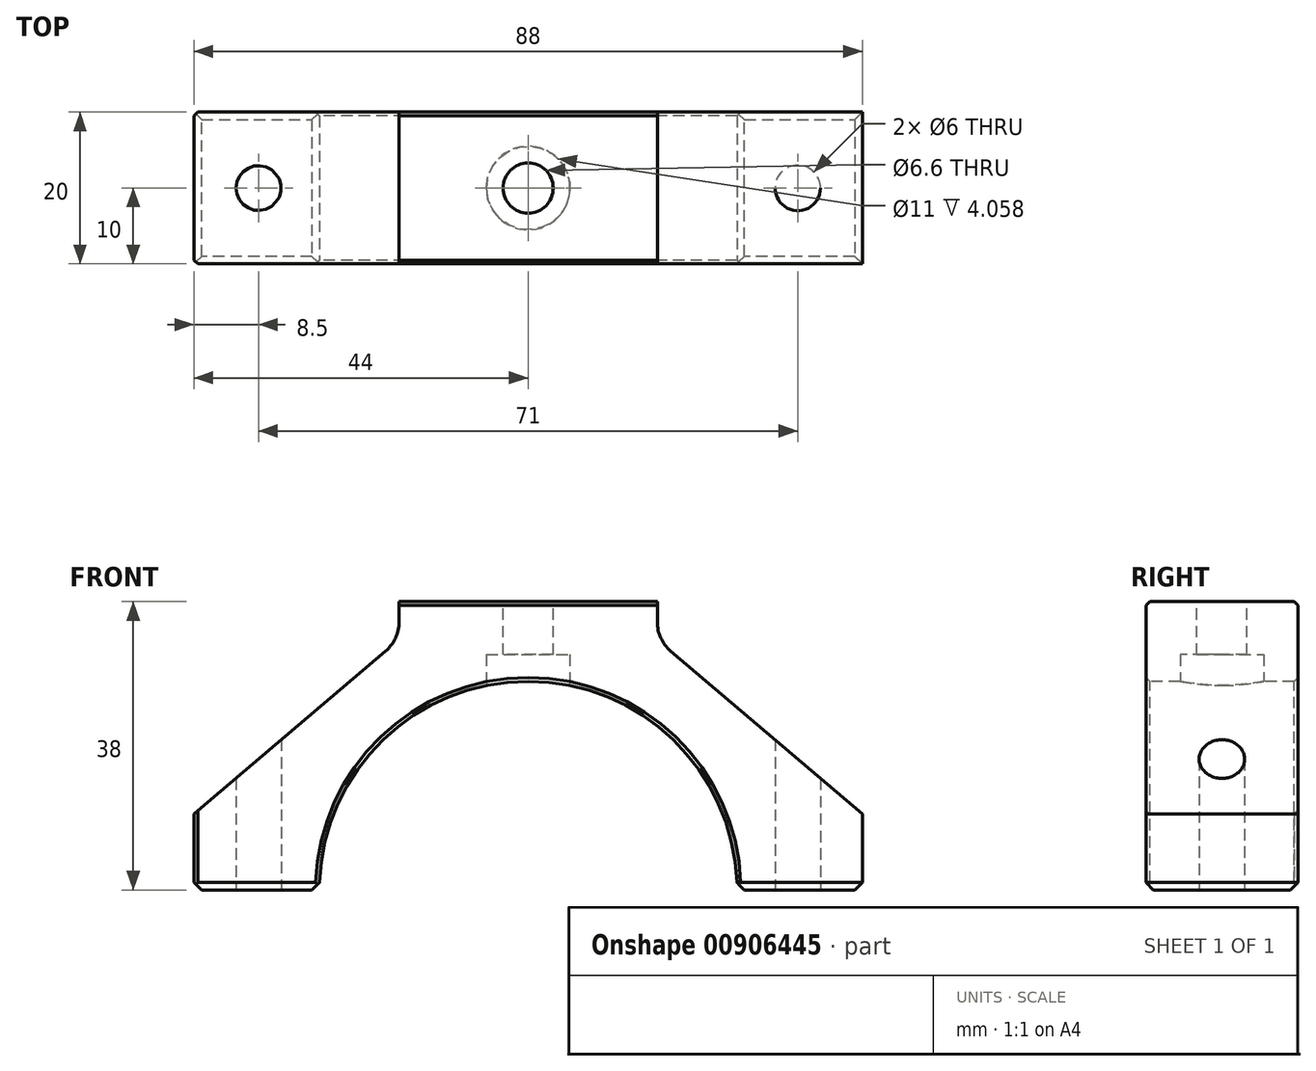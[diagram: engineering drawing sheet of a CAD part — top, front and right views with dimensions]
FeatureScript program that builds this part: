
annotation { "Feature Type Name" : "Feature", "Feature Type Description" : "" }
export const myFeature = defineFeature(function(context is Context, id is Id, definition is map)
    precondition{}
    {
        {
            var Q0;
            Q0=qCreatedBy(makeId("Front.planeOp"),FACE);
            var sketch = newSketch(context, id + "F0", { "sketchPlane" : qUnion([Q0])});
            skLineSegment(sketch, "E0", {"start": v(0, 0) * mm, "end": v(44, 0) * mm});
            skLineSegment(sketch, "E1", {"start": v(17, 38) * mm, "end": v(-17, 38) * mm});
            skLineSegment(sketch, "E2", {"start": v(-44, 10) * mm, "end": v(-44, 0) * mm});
            skLineSegment(sketch, "E3", {"start": v(-44, 0) * mm, "end": v(0, 0) * mm});
            skCircle(sketch, "E4", {"center": v(0, 0) * mm, "radius": 27.5 * mm});
            skLineSegment(sketch, "E5", {"start": v(44, 0) * mm, "end": v(44, 10) * mm});
            skLineSegment(sketch, "E6", {"start": v(17, 38) * mm, "end": v(44, 10) * mm});
            skLineSegment(sketch, "E7", {"start": v(-44, 10) * mm, "end": v(-17, 38) * mm});
            skLineSegment(sketch, "E8", {"start": v(-17, 38) * mm, "end": v(-17, 33) * mm});
            skLineSegment(sketch, "E9", {"start": v(-17, 33) * mm, "end": v(-44, 10) * mm});
            skLineSegment(sketch, "E10", {"start": v(17, 38) * mm, "end": v(17, 33) * mm});
            skLineSegment(sketch, "E11", {"start": v(17, 33) * mm, "end": v(44, 10) * mm});
            skSolve(sketch);
        }
        {
            var Q0;
            Q0=makeQuery(id+"F0.imprint","IMPRINT",FACE,{"disambiguationData":[TD([[makeQuery(id+"F0.imprint","IMPRINT",EDGE,{"derivedFrom":sQuery(id+"F0.wireOp",EDGE,"E1")}),1.0]])]});
            extrude(context, id + "F1", {"entities" : qUnion([Q0]), "oppositeDirection" : true, "depth" : 20 * mm, "offsetDistance" : 25 * mm});
        }
        {
            var Q0;
            Q0=makeQuery(id+"F1.opExtrude","SWEPT_FACE",FACE,{"disambiguationData":[OSD([sQuery(id+"F0.wireOp",EDGE,"E3")])]});
            var sketch = newSketch(context, id + "F2", { "sketchPlane" : qUnion([Q0])});
            skPoint(sketch, "E12", {"position": v(-35.5, -10) * mm});
            skPoint(sketch, "E13", {"position": v(35.5, -10) * mm});
            skSolve(sketch);
        }
        {
            var Q0;
            Q0=sQuery(id+"F2.wireOp",VERTEX,"E12");
            var Q1;
            Q1=sQuery(id+"F2.wireOp",VERTEX,"E13");
            var Q2;
            Q2=makeQuery(id+"F1.opExtrude","SWEPT_BODY",BODY,{"disambiguationData":[OSD([sQuery(id+"F0.wireOp",EDGE,"E0"),sQuery(id+"F0.wireOp",EDGE,"26qg7wP1-cfzZ-PcFu-JOlJ-KpqFD53kFSD1"),sQuery(id+"F0.wireOp",EDGE,"RVsKIFsQ-KtRt-3r3y-Fqtk-HxQzNuTVFL8h"),sQuery(id+"F0.wireOp",EDGE,"qqPmwvpG-DLSY-BAFD-hjqW-52uUpys1eQfQ"),sQuery(id+"F0.wireOp",EDGE,"E1"),sQuery(id+"F0.wireOp",EDGE,"qsKTKu1S-p0Ix-3YJR-Cw6W-Frjfaacasj22"),sQuery(id+"F0.wireOp",EDGE,"3hkLzmr7-WQ0R-AfxT-Muqp-fxqsySZg4Wku"),sQuery(id+"F0.wireOp",EDGE,"E2"),sQuery(id+"F0.wireOp",EDGE,"E3"),sQuery(id+"F0.wireOp",EDGE,"E4")])]});
            hole(context, id + "F3", {"style" : HoleStyle.SIMPLE, "endStyle" : HoleEndStyle.THROUGH, "holeDiameter" : 6 * mm, "majorDiameter" : 5 * mm, "isTappedThrough" : true, "tappedDepth" : 12 * mm, "tapClearance" : 3, "locations" : qUnion([Q0, Q1]), "scope" : qUnion([Q2])});
        }
        {
            var Q0;
            Q0=makeQuery(id+"F1.opExtrude","CAP_EDGE",EDGE,{"disambiguationData":[OSD([sQuery(id+"F0.wireOp",EDGE,"E0")])],"isStart":false});
            var Q1;
            Q1=makeQuery(id+"F1.opExtrude","SWEPT_EDGE",EDGE,{"disambiguationData":[OSD([sQuery(id+"F0.wireOp",EDGE,"E0"),sQuery(id+"F0.wireOp",EDGE,"26qg7wP1-cfzZ-PcFu-JOlJ-KpqFD53kFSD1")])]});
            var Q2;
            Q2=makeQuery(id+"F1.opExtrude","CAP_EDGE",EDGE,{"disambiguationData":[OSD([sQuery(id+"F0.wireOp",EDGE,"E3")])],"isStart":false});
            var Q3;
            Q3=makeQuery(id+"F1.opExtrude","SWEPT_EDGE",EDGE,{"disambiguationData":[OSD([sQuery(id+"F0.wireOp",EDGE,"E3"),sQuery(id+"F0.wireOp",EDGE,"E4")])]});
            var Q4;
            Q4=makeQuery(id+"F1.opExtrude","CAP_EDGE",EDGE,{"disambiguationData":[OSD([sQuery(id+"F0.wireOp",EDGE,"E3")])],"isStart":true});
            var Q5;
            Q5=makeQuery(id+"F1.opExtrude","SWEPT_EDGE",EDGE,{"disambiguationData":[OSD([sQuery(id+"F0.wireOp",EDGE,"E2"),sQuery(id+"F0.wireOp",EDGE,"E3")])]});
            var Q6;
            Q6=makeQuery(id+"F1.opExtrude","SWEPT_EDGE",EDGE,{"disambiguationData":[OSD([sQuery(id+"F0.wireOp",EDGE,"E0"),sQuery(id+"F0.wireOp",EDGE,"E4")])]});
            var Q7;
            Q7=makeQuery(id+"F1.opExtrude","CAP_EDGE",EDGE,{"disambiguationData":[OSD([sQuery(id+"F0.wireOp",EDGE,"E0")])],"isStart":true});
            chamfer(context, id + "F4", {"entities" : qUnion([Q0, Q1, Q2, Q3, Q4, Q5, Q6, Q7]), "width" : 1 * mm, "tangentPropagation" : true});
        }
        {
            var Q0;
            Q0=makeQuery(id+"F1.opExtrude","CAP_EDGE",EDGE,{"disambiguationData":[OSD([sQuery(id+"F0.wireOp",EDGE,"26qg7wP1-cfzZ-PcFu-JOlJ-KpqFD53kFSD1")])],"isStart":false});
            var Q1;
            Q1=makeQuery(id+"F1.opExtrude","CAP_EDGE",EDGE,{"disambiguationData":[OSD([sQuery(id+"F0.wireOp",EDGE,"26qg7wP1-cfzZ-PcFu-JOlJ-KpqFD53kFSD1")])],"isStart":true});
            var Q2;
            Q2=makeQuery(id+"F1.opExtrude","SWEPT_EDGE",EDGE,{"disambiguationData":[OSD([sQuery(id+"F0.wireOp",EDGE,"26qg7wP1-cfzZ-PcFu-JOlJ-KpqFD53kFSD1"),sQuery(id+"F0.wireOp",EDGE,"RVsKIFsQ-KtRt-3r3y-Fqtk-HxQzNuTVFL8h")])]});
            var Q3;
            Q3=makeQuery(id+"F1.opExtrude","CAP_EDGE",EDGE,{"disambiguationData":[OSD([sQuery(id+"F0.wireOp",EDGE,"RVsKIFsQ-KtRt-3r3y-Fqtk-HxQzNuTVFL8h")])],"isStart":false});
            var Q4;
            Q4=makeQuery(id+"F1.opExtrude","CAP_EDGE",EDGE,{"disambiguationData":[OSD([sQuery(id+"F0.wireOp",EDGE,"RVsKIFsQ-KtRt-3r3y-Fqtk-HxQzNuTVFL8h")])],"isStart":true});
            var Q5;
            Q5=makeQuery(id+"F1.opExtrude","CAP_EDGE",EDGE,{"disambiguationData":[OSD([sQuery(id+"F0.wireOp",EDGE,"qqPmwvpG-DLSY-BAFD-hjqW-52uUpys1eQfQ")])],"isStart":true});
            var Q6;
            Q6=makeQuery(id+"F1.opExtrude","CAP_EDGE",EDGE,{"disambiguationData":[OSD([sQuery(id+"F0.wireOp",EDGE,"qqPmwvpG-DLSY-BAFD-hjqW-52uUpys1eQfQ")])],"isStart":false});
            var Q7;
            Q7=makeQuery(id+"F1.opExtrude","CAP_EDGE",EDGE,{"disambiguationData":[OSD([sQuery(id+"F0.wireOp",EDGE,"E1")])],"isStart":false});
            var Q8;
            Q8=makeQuery(id+"F1.opExtrude","CAP_EDGE",EDGE,{"disambiguationData":[OSD([sQuery(id+"F0.wireOp",EDGE,"E1")])],"isStart":true});
            var Q9;
            Q9=makeQuery(id+"F1.opExtrude","CAP_EDGE",EDGE,{"disambiguationData":[OSD([sQuery(id+"F0.wireOp",EDGE,"qsKTKu1S-p0Ix-3YJR-Cw6W-Frjfaacasj22")])],"isStart":false});
            var Q10;
            Q10=makeQuery(id+"F1.opExtrude","CAP_EDGE",EDGE,{"disambiguationData":[OSD([sQuery(id+"F0.wireOp",EDGE,"E4")])],"isStart":false});
            var Q11;
            Q11=makeQuery(id+"F1.opExtrude","CAP_EDGE",EDGE,{"disambiguationData":[OSD([sQuery(id+"F0.wireOp",EDGE,"E2")])],"isStart":false});
            var Q12;
            Q12=makeQuery(id+"F1.opExtrude","CAP_EDGE",EDGE,{"disambiguationData":[OSD([sQuery(id+"F0.wireOp",EDGE,"3hkLzmr7-WQ0R-AfxT-Muqp-fxqsySZg4Wku")])],"isStart":false});
            var Q13;
            Q13=makeQuery(id+"F1.opExtrude","SWEPT_EDGE",EDGE,{"disambiguationData":[OSD([sQuery(id+"F0.wireOp",EDGE,"3hkLzmr7-WQ0R-AfxT-Muqp-fxqsySZg4Wku"),sQuery(id+"F0.wireOp",EDGE,"E2")])]});
            var Q14;
            Q14=makeQuery(id+"F1.opExtrude","CAP_EDGE",EDGE,{"disambiguationData":[OSD([sQuery(id+"F0.wireOp",EDGE,"3hkLzmr7-WQ0R-AfxT-Muqp-fxqsySZg4Wku")])],"isStart":true});
            var Q15;
            Q15=makeQuery(id+"F1.opExtrude","CAP_EDGE",EDGE,{"disambiguationData":[OSD([sQuery(id+"F0.wireOp",EDGE,"E4")])],"isStart":true});
            var Q16;
            Q16=makeQuery(id+"F1.opExtrude","CAP_EDGE",EDGE,{"disambiguationData":[OSD([sQuery(id+"F0.wireOp",EDGE,"qsKTKu1S-p0Ix-3YJR-Cw6W-Frjfaacasj22")])],"isStart":true});
            var Q17;
            Q17=makeQuery(id+"F1.opExtrude","CAP_EDGE",EDGE,{"disambiguationData":[OSD([sQuery(id+"F0.wireOp",EDGE,"E2")])],"isStart":true});
            chamfer(context, id + "F5", {"entities" : qUnion([Q0, Q1, Q2, Q3, Q4, Q5, Q6, Q7, Q8, Q9, Q10, Q11, Q12, Q13, Q14, Q15, Q16, Q17]), "width" : 0.5 * mm, "tangentPropagation" : true});
        }
        {
            var Q0;
            Q0=makeQuery(id+"F1.opExtrude","SWEPT_FACE",FACE,{"disambiguationData":[OSD([sQuery(id+"F0.wireOp",EDGE,"E1")])]});
            var sketch = newSketch(context, id + "F6", { "sketchPlane" : qUnion([Q0])});
            skPoint(sketch, "E14", {"position": v(0, 10) * mm});
            skSolve(sketch);
        }
        {
            var Q0;
            Q0=sQuery(id+"F6.wireOp",VERTEX,"E14");
            var Q1;
            Q1=makeQuery(id+"F1.opExtrude","SWEPT_BODY",BODY,{"disambiguationData":[OSD([sQuery(id+"F0.wireOp",EDGE,"E0"),sQuery(id+"F0.wireOp",EDGE,"E1"),sQuery(id+"F0.wireOp",EDGE,"E2"),sQuery(id+"F0.wireOp",EDGE,"E3"),sQuery(id+"F0.wireOp",EDGE,"E4"),sQuery(id+"F0.wireOp",EDGE,"E5"),sQuery(id+"F0.wireOp",EDGE,"E6"),sQuery(id+"F0.wireOp",EDGE,"E7")])]});
            hole(context, id + "F7", {"style" : HoleStyle.SIMPLE, "endStyle" : HoleEndStyle.THROUGH, "standardTappedOrClearance" : lookupTablePath({ "fit" : "Normal", "standard" : "ISO", "size" : "M6", "type" : "Clearance" }), "standardBlindInLast" : lookupTablePath({ "fit" : "Normal", "standard" : "ISO", "size" : "M6", "type" : "Clearance" }), "holeDiameter" : 6.6 * mm, "majorDiameter" : 5 * mm, "isTappedThrough" : true, "tappedDepth" : 12 * mm, "tapClearance" : 3, "locations" : qUnion([Q0]), "scope" : qUnion([Q1])});
        }
        {
            var Q0;
            Q0=qCreatedBy(makeId("Top.planeOp"),FACE);
            cPlane(context, id + "F8", {"entities" : qUnion([Q0]), "cplaneType" : CPlaneType.OFFSET, "offset" : 27.5 * mm, "width" : 150 * mm, "height" : 150 * mm});
        }
        {
            var Q0;
            Q0=qCreatedBy(id+"F8.planeOp",FACE);
            var sketch = newSketch(context, id + "F9", { "sketchPlane" : qUnion([Q0])});
            skPoint(sketch, "E15", {"position": v(0, 10) * mm});
            skCircle(sketch, "E16", {"center": v(0, 10) * mm, "radius": 5.5 * mm});
            skSolve(sketch);
        }
        {
            var Q0;
            Q0=makeQuery(id+"F9.imprint","IMPRINT",FACE,{"disambiguationData":[TD([[makeQuery(id+"F9.imprint","IMPRINT",EDGE,{"derivedFrom":sQuery(id+"F9.wireOp",EDGE,"E16")}),1.0]])]});
            extrude(context, id + "F10", {"entities" : qUnion([Q0]), "operationType" : NewBodyOperationType.REMOVE, "endBound" : BoundingType.SYMMETRIC, "depth" : 7 * mm, "offsetDistance" : 25 * mm});
        }
        {
            var Q0;
            Q0=makeQuery(id+"F1.opExtrude","SWEPT_EDGE",EDGE,{"disambiguationData":[OSD([sQuery(id+"F0.wireOp",EDGE,"E8"),sQuery(id+"F0.wireOp",EDGE,"E9")])]});
            var Q1;
            Q1=makeQuery(id+"F1.opExtrude","SWEPT_EDGE",EDGE,{"disambiguationData":[OSD([sQuery(id+"F0.wireOp",EDGE,"E10"),sQuery(id+"F0.wireOp",EDGE,"E11")])]});
            fillet(context, id + "F11", {"entities" : qUnion([Q0, Q1]), "radius" : 5 * mm, "tangentPropagation" : true, "allowEdgeOverflow" : false});
        }
    });
